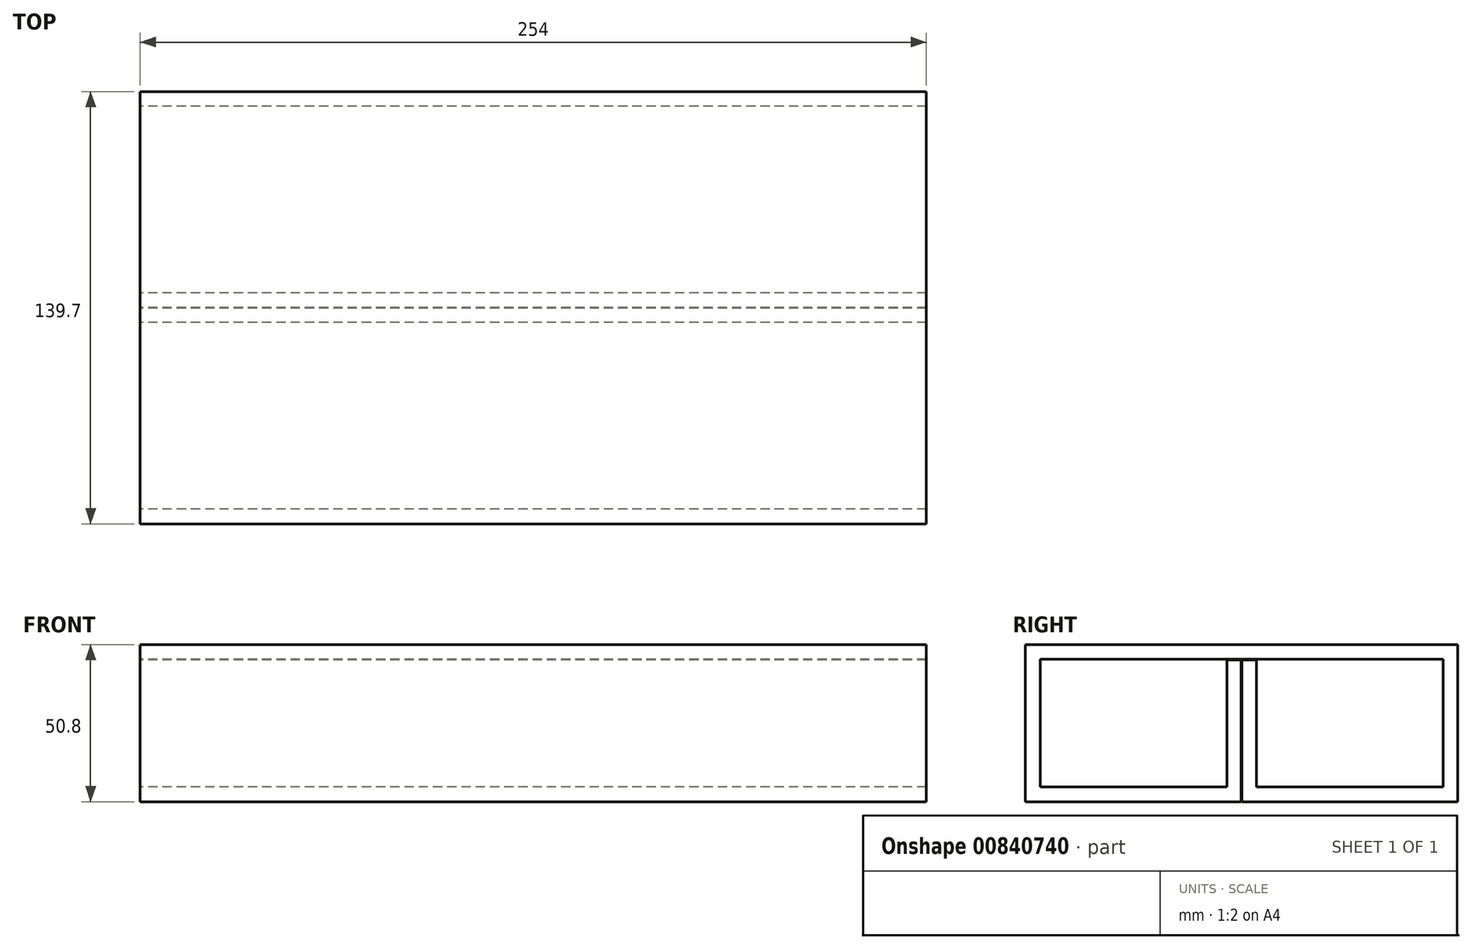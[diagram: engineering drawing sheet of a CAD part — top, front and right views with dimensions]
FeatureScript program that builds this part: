
annotation { "Feature Type Name" : "Feature", "Feature Type Description" : "" }
export const myFeature = defineFeature(function(context is Context, id is Id, definition is map)
    precondition{}
    {
        {
            var Q0;
            Q0=qCreatedBy(makeId("Right.planeOp"),FACE);
            var sketch = newSketch(context, id + "F0", { "sketchPlane" : qUnion([Q0])});
            skLineSegment(sketch, "E0", {"start": v(0, 0) * mm, "end": v(0, 126.35) * mm, "construction": true});
            skLineSegment(sketch, "E1.bottom", {"start": v(-69.85, 50.8) * mm, "end": v(69.85, 50.8) * mm});
            skLineSegment(sketch, "E1.top", {"start": v(-69.85, 0) * mm, "end": v(-0.13, 0) * mm});
            skLineSegment(sketch, "E1.left", {"start": v(-69.85, 50.8) * mm, "end": v(-69.85, 0) * mm});
            skLineSegment(sketch, "E2.0", {"start": v(-65.09, 46.04) * mm, "end": v(65.09, 46.04) * mm});
            skLineSegment(sketch, "E2.1", {"start": v(-65.09, 46.04) * mm, "end": v(-65.09, 4.76) * mm});
            skLineSegment(sketch, "E2.2", {"start": v(-65.09, 4.76) * mm, "end": v(-4.76, 4.76) * mm});
            skLineSegment(sketch, "E2.3", {"start": v(-4.76, 45.78) * mm, "end": v(-4.76, 4.76) * mm});
            skLineSegment(sketch, "E3.MirrorCS", {"start": v(69.85, 50.8) * mm, "end": v(69.85, 0) * mm});
            skLineSegment(sketch, "E4.MirrorCS", {"start": v(4.76, 45.78) * mm, "end": v(4.76, 4.76) * mm});
            skLineSegment(sketch, "E5.MirrorCS", {"start": v(65.09, 4.76) * mm, "end": v(4.76, 4.76) * mm});
            skLineSegment(sketch, "E6.MirrorCS", {"start": v(65.09, 46.04) * mm, "end": v(65.09, 4.76) * mm});
            skLineSegment(sketch, "E7.left", {"start": v(-0.13, 0) * mm, "end": v(-0.13, 45.78) * mm});
            skLineSegment(sketch, "E7.right", {"start": v(0.13, 0) * mm, "end": v(0.13, 45.78) * mm});
            skLineSegment(sketch, "E8.trimOffspring", {"start": v(0.13, 0) * mm, "end": v(69.85, 0) * mm});
            skLineSegment(sketch, "E9", {"start": v(-4.76, 45.78) * mm, "end": v(-0.13, 45.78) * mm});
            skPoint(sketch, "E10.orphan", {"position": v(4.76, 46.04) * mm});
            skLineSegment(sketch, "E11.trimOffspring", {"start": v(0.13, 45.78) * mm, "end": v(4.76, 45.78) * mm});
            skPoint(sketch, "E12.orphan", {"position": v(-4.76, 46.04) * mm});
            skSolve(sketch);
        }
        {
            var Q0;
            Q0=qSketchRegion(id+"F0",true);
            extrude(context, id + "F1", {"entities" : qUnion([Q0]), "endBound" : BoundingType.SYMMETRIC, "depth" : 254 * mm, "offsetDistance" : 25.4 * mm});
        }
    });
